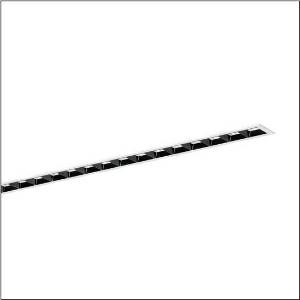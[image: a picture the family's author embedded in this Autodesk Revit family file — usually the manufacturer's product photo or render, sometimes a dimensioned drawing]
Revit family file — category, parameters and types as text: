
# Revit family: silica_r__21_51mx14tctaw_e0ea
name_source: partatom
category: Lighting Fixtures
units: mm (PartAtom-declared; Revit-internal decimal feet)

## family parameters
Cut with Voids When Loaded = No
Host = Face
Light Source = No
Part Type = Normal
Room Calculation Point = No
Round Connector Dimension = Use Diameter
Shared = No

## types (1)
- --- (1 x LED, 8200 lm, 81.1 W, 6500K)
    Apparent Load = 81 VA
    CIE Flux Codes = 74 94 99 100 100
    Color Rendering = 80
    Color Temperature = 6500K
    Default Elevation = 1800 mm
    Description = Silica® 21, office luminaire, primary light control with darklight reflector, of PMMA, black, light emission: direct distribution, primary light characteristic: asymmetric, installation type: recessed, LED, rated luminous flux: 8.200lm, luminous efficacy: 96lm/W, light colour: 8tw, colour temperature: 2700..6500K, with terminal, 3+2-pole, max. 2.5mm², mains connection: 220..240V, AC, 50/60Hz, rated input power: 85.2W, luminaire housing, of aluminium, traffic white (RAL 9016), length: 3.028mm, width: 79mm, height: 53mm, protection rating (complete): IP20, insulation class (complete): insulation class I (protective earthing), certification: CE, permissible operating ambient temperature: 0..+35°C, standard: EN 50419, packaging unit: 1 piece
    Height = 0 mm  [stored 0 ft]
    Lamp = 1 x LED
    Lamp Light Flux = 8200 lm
    Lamp Power = 81.1 W
    Lamp count = 1
    Length = 3027 mm
    Luminous efficacy = 101 lm/W
    Manufacturer = Siteco
    ModVariant = No
    Model = 51MX14TCTAW
    Mounting Place = Ceiling
    Mounting Type = Recessed
    Number of Poles = 1
    OnlyDefault = Yes
    Power Factor = 1
    Product Name = Silica® 21
    Product group = office luminaire | ceiling recessed
    ProductGroupID = 400
    Protection Class = Protection class I
    Protection Degree = IP 20
    RLX_Detail_Level = 1
    RlxData = <blob elided: 59621 chars, md5=af0746ab>
    Socket = socket
    Standby Power = 0 W
    System Light Flux = 8200 lm
    System Power = 81 W
    Type Comments = individual setting
    Type Image = l_1251632.jpg
    URL = http://relux.com
    VarID = @adj_046113
    Voltage = 0 V
    Weight = 0.00 kg
    Width = 79 mm

note: [stored X ft] marks values corroborated as IEEE doubles in the binary element streams (Revit-internal decimal feet)

## geometry (parser evidence)
native form markers: Blend x4, Sweep x10
no freeform markers — native parametric forms only
